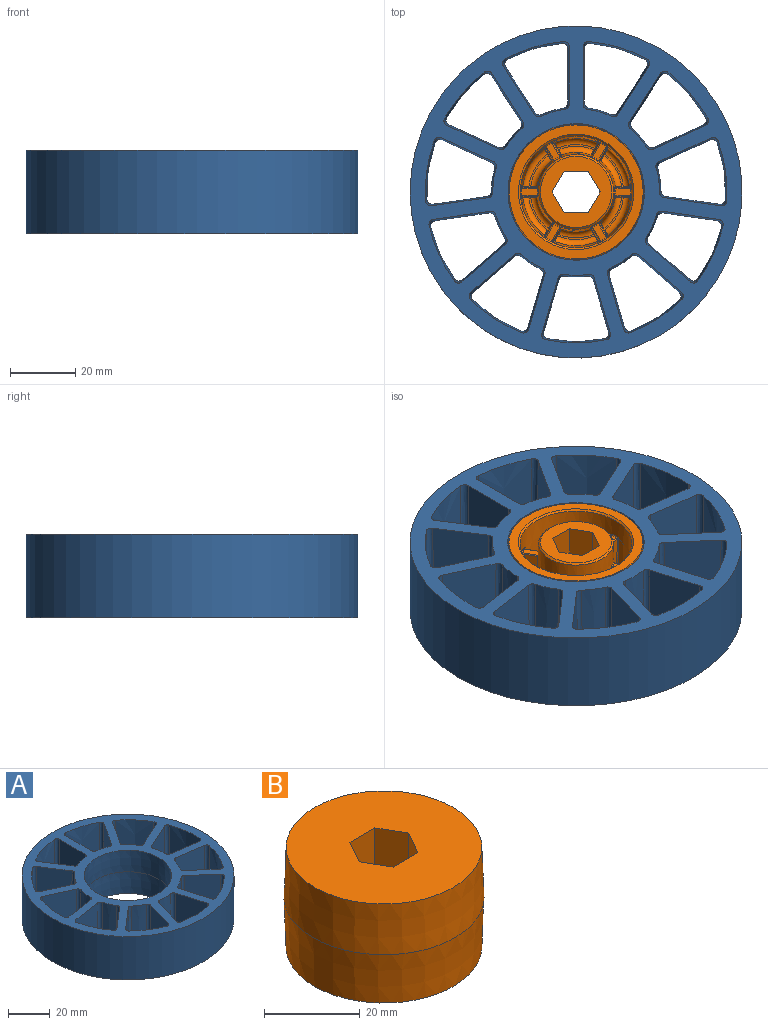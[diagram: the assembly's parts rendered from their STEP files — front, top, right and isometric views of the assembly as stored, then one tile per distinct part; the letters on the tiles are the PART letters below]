
ASSEMBLY  parts=2 mates=1
PART A: 93 faces, bbox 101.7x101.7x25.8 mm
  f0: cylinder r=50.8mm len=101.6mm, axis (0,0,-1), area 8107.3mm2, adj f25,f27
  f1: cone r=20.96mm half-angle=0.3deg, axis (0,0,1), area 1669.7mm2, adj f2,f27
  f2: cone r=20.89mm half-angle=0.3deg, axis (0,0,-1), area 1669.7mm2, adj f1,f25
  f3: cone r=45.72mm half-angle=1deg, axis (0,0,1), area 460.8mm2, adj f25,f27,f58,f59
  f4: cone r=25.97mm half-angle=1deg, axis (0,0,-1), area 186.1mm2, adj f25,f27,f80,f81
  f5: cone r=25.97mm half-angle=1deg, axis (0,0,-1), area 186.2mm2, adj f25,f27,f88,f89
  f6: cone r=45.72mm half-angle=1deg, axis (0,0,1), area 460.8mm2, adj f25,f27,f90,f91
  f7: cone r=45.72mm half-angle=1deg, axis (0,0,1), area 460.8mm2, adj f25,f27,f82,f83
  f8: cone r=25.97mm half-angle=1deg, axis (0,0,-1), area 186.2mm2, adj f25,f27,f76,f77
  f9: cone r=45.72mm half-angle=1deg, axis (0,0,1), area 460.8mm2, adj f25,f27,f78,f79
  f10: cone r=25.97mm half-angle=1deg, axis (0,0,-1), area 186.2mm2, adj f25,f27,f72,f73
  f11: cone r=45.72mm half-angle=1deg, axis (0,0,1), area 460.8mm2, adj f25,f27,f74,f75
  f12: cone r=25.97mm half-angle=1deg, axis (0,0,-1), area 186.2mm2, adj f25,f27,f68,f69
  f13: cone r=45.72mm half-angle=1deg, axis (0,0,1), area 460.8mm2, adj f25,f27,f70,f71
  f14: cone r=25.97mm half-angle=1deg, axis (0,0,-1), area 186.2mm2, adj f25,f27,f64,f65
  f15: cone r=45.72mm half-angle=1deg, axis (0,0,1), area 460.8mm2, adj f25,f27,f66,f67
  f16: cone r=25.97mm half-angle=1deg, axis (0,0,-1), area 186.2mm2, adj f25,f27,f60,f61
  f17: cone r=45.72mm half-angle=1deg, axis (0,0,1), area 460.8mm2, adj f25,f27,f62,f63
  f18: cone r=25.97mm half-angle=1deg, axis (0,0,-1), area 186.2mm2, adj f25,f27,f56,f57
  f19: cone r=25.97mm half-angle=1deg, axis (0,0,-1), area 186.2mm2, adj f25,f27,f52,f53
  f20: cone r=45.72mm half-angle=1deg, axis (0,0,1), area 460.8mm2, adj f25,f27,f54,f55
  f21: cone r=25.97mm half-angle=1deg, axis (0,0,-1), area 186.2mm2, adj f25,f27,f49,f50
  f22: cone r=45.72mm half-angle=1deg, axis (0,0,1), area 460.8mm2, adj f25,f27,f51,f92
  f23: plane 25.4x17.56mm, normal (1,0,0.02), area 435mm2, adj f25,f27,f85,f86
  f24: plane 25.4x17.56mm, normal (-1,0,0.02), area 435mm2, adj f25,f27,f50,f92
  f25: plane 101.66x101.66mm, normal (0,0,1), area 3063.9mm2, adj f0,f2,f3,f4,f5,f6,f7,f8
  f26: cone r=25.97mm half-angle=1deg, axis (0,0,-1), area 186.2mm2, adj f25,f27,f86,f87
  f27: plane 101.66x101.66mm, normal (0,0,-1), area 3415.8mm2, adj f0,f1,f3,f4,f5,f6,f7,f8
  f28: cone r=45.72mm half-angle=1deg, axis (0,0,1), area 460.8mm2, adj f25,f27,f84,f85
  f29: plane 25.4x14.77mm, normal (0.84,0.54,0.02), area 435mm2, adj f25,f27,f49,f51
  f30: plane 25.4x14.77mm, normal (-0.84,-0.54,0.02), area 435mm2, adj f25,f27,f53,f54
  f31: plane 25.4x15.97mm, normal (0.42,0.91,0.02), area 435mm2, adj f25,f27,f52,f55
  f32: plane 25.4x15.97mm, normal (-0.42,-0.91,0.02), area 435mm2, adj f25,f27,f57,f58
  f33: plane 25.4x17.38mm, normal (-0.14,0.99,0.02), area 435mm2, adj f25,f27,f56,f59
  f34: plane 25.4x17.38mm, normal (0.14,-0.99,0.02), area 435mm2, adj f25,f27,f61,f62
  f35: plane 25.4x13.27mm, normal (-0.65,0.76,0.02), area 435mm2, adj f25,f27,f60,f63
  f36: plane 25.4x13.27mm, normal (0.65,-0.76,0.02), area 435mm2, adj f25,f27,f65,f66
  f37: plane 25.4x16.85mm, normal (-0.96,0.28,0.02), area 435mm2, adj f25,f27,f64,f67
  f38: plane 25.4x16.85mm, normal (0.96,-0.28,0.02), area 435mm2, adj f25,f27,f69,f70
  f39: plane 25.4x16.85mm, normal (-0.96,-0.28,0.02), area 435mm2, adj f25,f27,f68,f71
  f40: plane 25.4x16.85mm, normal (0.96,0.28,0.02), area 435mm2, adj f25,f27,f73,f74
  f41: plane 25.4x13.27mm, normal (-0.65,-0.76,0.02), area 435mm2, adj f25,f27,f72,f75
  f42: plane 25.4x13.27mm, normal (0.65,0.76,0.02), area 435mm2, adj f25,f27,f77,f78
  f43: plane 25.4x17.38mm, normal (-0.14,-0.99,0.02), area 435mm2, adj f25,f27,f76,f79
  f44: plane 25.4x17.38mm, normal (0.14,0.99,0.02), area 435mm2, adj f25,f27,f81,f82
  f45: plane 25.4x15.97mm, normal (0.42,-0.91,0.02), area 435mm2, adj f25,f27,f80,f83
  f46: plane 25.4x15.97mm, normal (-0.42,0.91,0.02), area 435mm2, adj f25,f27,f89,f90
  f47: plane 25.4x14.77mm, normal (0.84,-0.54,0.02), area 435mm2, adj f25,f27,f88,f91
  f48: plane 25.4x14.77mm, normal (-0.84,0.54,0.02), area 435mm2, adj f25,f27,f84,f87
  f49: bspline ~25.41x2.15mm, area 57.6mm2, adj f21,f25,f27,f29
  f50: bspline ~25.41x1.96mm, area 57.6mm2, adj f21,f24,f25,f27
  f51: bspline ~25.41x2.43mm, area 66.9mm2, adj f22,f25,f27,f29
  f52: bspline ~25.41x2.17mm, area 57.6mm2, adj f19,f25,f27,f31
  f53: bspline ~25.41x2.15mm, area 57.6mm2, adj f19,f25,f27,f30
  f54: bspline ~25.75x2.43mm, area 66.9mm2, adj f20,f25,f27,f30
  f55: bspline ~25.75x2.44mm, area 66.9mm2, adj f20,f25,f27,f31
  f56: bspline ~25.73x1.95mm, area 57.6mm2, adj f18,f25,f27,f33
  f57: bspline ~25.73x2.13mm, area 57.6mm2, adj f18,f25,f27,f32
  f58: bspline ~25.75x2.41mm, area 66.9mm2, adj f3,f25,f27,f32
  f59: bspline ~25.41x2.23mm, area 66.9mm2, adj f3,f25,f27,f33
  f60: bspline ~25.73x2.13mm, area 57.6mm2, adj f16,f25,f27,f35
  f61: bspline ~25.41x2.07mm, area 57.6mm2, adj f16,f25,f27,f34
  f62: bspline ~25.41x2.31mm, area 66.9mm2, adj f17,f25,f27,f34
  f63: bspline ~25.75x2.4mm, area 66.9mm2, adj f17,f25,f27,f35
  f64: bspline ~25.73x2.14mm, area 57.6mm2, adj f14,f25,f27,f37
  f65: bspline ~25.73x2.09mm, area 57.6mm2, adj f14,f25,f27,f36
  f66: bspline ~25.41x2.36mm, area 66.9mm2, adj f15,f25,f27,f36
  f67: bspline ~25.75x2.4mm, area 66.9mm2, adj f15,f25,f27,f37
  f68: bspline ~25.41x2.05mm, area 57.6mm2, adj f12,f25,f27,f39
  f69: bspline ~25.41x2.05mm, area 57.6mm2, adj f12,f25,f27,f38
  f70: bspline ~25.41x2.34mm, area 66.9mm2, adj f13,f25,f27,f38
  f71: bspline ~25.41x2.34mm, area 66.9mm2, adj f13,f25,f27,f39
  f72: bspline ~25.73x2.09mm, area 57.6mm2, adj f10,f25,f27,f41
  f73: bspline ~25.73x2.14mm, area 57.6mm2, adj f10,f25,f27,f40
  f74: bspline ~25.75x2.4mm, area 66.9mm2, adj f11,f25,f27,f40
  f75: bspline ~25.41x2.36mm, area 66.9mm2, adj f11,f25,f27,f41
  f76: bspline ~25.41x2.07mm, area 57.6mm2, adj f8,f25,f27,f43
  f77: bspline ~25.73x2.13mm, area 57.6mm2, adj f8,f25,f27,f42
  f78: bspline ~25.75x2.4mm, area 66.9mm2, adj f9,f25,f27,f42
  f79: bspline ~25.41x2.31mm, area 66.9mm2, adj f9,f25,f27,f43
  f80: bspline ~25.73x2.13mm, area 57.6mm2, adj f4,f25,f27,f45
  f81: bspline ~25.41x1.94mm, area 57.6mm2, adj f4,f25,f27,f44
  f82: bspline ~25.41x2.23mm, area 66.9mm2, adj f7,f25,f27,f44
  f83: bspline ~25.75x2.41mm, area 66.9mm2, adj f7,f25,f27,f45
  f84: bspline ~25.41x2.43mm, area 66.9mm2, adj f25,f27,f28,f48
  f85: bspline ~25.41x2.18mm, area 66.9mm2, adj f23,f25,f27,f28
  f86: bspline ~25.41x1.96mm, area 57.6mm2, adj f23,f25,f26,f27
  f87: bspline ~25.41x2.15mm, area 57.6mm2, adj f25,f26,f27,f48
  f88: bspline ~25.41x2.15mm, area 57.6mm2, adj f5,f25,f27,f47
  f89: bspline ~25.41x2.17mm, area 57.6mm2, adj f5,f25,f27,f46
  f90: bspline ~25.75x2.44mm, area 66.9mm2, adj f6,f25,f27,f46
  f91: bspline ~25.75x2.43mm, area 66.9mm2, adj f6,f25,f27,f47
  f92: bspline ~25.41x2.18mm, area 66.9mm2, adj f22,f24,f25,f27
PART B: 159 faces, bbox 41.9x41.9x25.4 mm
  f0: torus R=16.68mm, axis (0,0,1), area 0.8mm2, adj f6,f31,f40,f45
  f1: torus R=11.9mm, axis (0,0,1), area 0.8mm2, adj f7,f31,f36,f41
  f2: cone r=20.24mm half-angle=2deg, axis (0,0,-1), area 1655.4mm2, adj f3,f25
  f3: cone r=20.96mm half-angle=2deg, axis (0,0,1), area 1655.4mm2, adj f2,f26
  f4: cone r=10.9mm half-angle=47deg, axis (0,0,1), area 52.3mm2, adj f7,f24
  f5: cone r=17.13mm half-angle=45deg, axis (0,0,-1), area 81.3mm2, adj f6,f26
  f6: cone r=16.46mm half-angle=2deg, axis (0,0,-1), area 1757.7mm2, adj f0,f5,f9,f12,f15,f18,f21,f27
  f7: cone r=11.43mm half-angle=2deg, axis (0,0,1), area 1163.6mm2, adj f1,f4,f8,f11,f14,f17,f20,f23
  f8: torus R=14.02mm, axis (0,0,-1), area 29mm2, adj f7,f10,f32,f146
  f9: torus R=14.55mm, axis (0,0,-1), area 37.6mm2, adj f6,f10,f35,f151
  f10: plane 9.83x5.94mm, normal (0,0,-1), area 6mm2, adj f8,f9,f33,f149
  f11: torus R=14.02mm, axis (0,0,-1), area 29mm2, adj f7,f13,f128,f135
  f12: torus R=14.55mm, axis (0,0,-1), area 37.6mm2, adj f6,f13,f133,f138
  f13: plane 11.35x1.61mm, normal (0,0,-1), area 6mm2, adj f11,f12,f131,f136
  f14: torus R=14.02mm, axis (0,0,-1), area 29mm2, adj f7,f16,f110,f117
  f15: torus R=14.55mm, axis (0,0,-1), area 37.6mm2, adj f6,f16,f115,f120
  f16: plane 9.83x5.94mm, normal (0,0,-1), area 6mm2, adj f14,f15,f113,f118
  f17: torus R=14.02mm, axis (0,0,-1), area 29mm2, adj f7,f19,f92,f99
  f18: torus R=14.55mm, axis (0,0,-1), area 37.6mm2, adj f6,f19,f97,f102
  f19: plane 9.83x5.94mm, normal (0,0,-1), area 6mm2, adj f17,f18,f95,f100
  f20: torus R=14.02mm, axis (0,0,-1), area 29mm2, adj f7,f22,f74,f81
  f21: torus R=14.55mm, axis (0,0,-1), area 37.6mm2, adj f6,f22,f79,f84
  f22: plane 11.35x1.61mm, normal (0,0,-1), area 6mm2, adj f20,f21,f77,f82
  f23: torus R=14.02mm, axis (0,0,-1), area 29mm2, adj f7,f28,f42,f63
  f24: plane 21.81x21.81mm, normal (0,0,-1), area 232.7mm2, adj f4,f153,f154,f155,f156,f157,f158
  f25: plane 41.02x41.02mm, normal (0,0,1), area 1180.9mm2, adj f2,f153,f154,f155,f156,f157,f158
  f26: plane 41.02x41.02mm, normal (0,0,-1), area 342.7mm2, adj f3,f5
  f27: torus R=14.55mm, axis (0,0,-1), area 37.6mm2, adj f6,f28,f46,f66
  f28: plane 9.83x5.94mm, normal (0,0,-1), area 6mm2, adj f23,f27,f44,f64
  f29: plane 14.75x4.78mm, normal (0,-1,-0.02), area 61.7mm2, adj f39,f42,f43,f44,f46,f47
  f30: plane 14.74x4.78mm, normal (0,1,-0.02), area 61.7mm2, adj f32,f33,f34,f35,f37,f38
  f31: plane 4.82x2.04mm, normal (0,0,-1), area 9.8mm2, adj f0,f1,f38,f43
  f32: bspline ~1.91x1.84mm, area 1mm2, adj f8,f30,f33,f34
  f33: cylinder r=0.25mm len=0.53mm, axis (-1,0,0), area 0.2mm2, adj f10,f30,f32,f35
  f34: bspline ~13.15x0.68mm, area 4.8mm2, adj f7,f30,f32,f36
  f35: bspline ~1.95x1.85mm, area 1.2mm2, adj f9,f30,f33,f37
  f36: bspline ~0.5x0.5mm, area 0.2mm2, adj f1,f7,f34,f38
  f37: bspline ~13.15x0.74mm, area 5.6mm2, adj f6,f30,f35,f40
  f38: cylinder r=0.25mm len=4.83mm, axis (-1,0,0), area 1.9mm2, adj f30,f31,f36,f40
  f39: cylinder r=0.25mm len=13.15mm, axis (0.03,-0.02,1), area 4.8mm2, adj f7,f29,f41,f42
  f40: bspline ~0.53x0.51mm, area 0.2mm2, adj f0,f6,f37,f38
  f41: bspline ~0.5x0.5mm, area 0.2mm2, adj f1,f7,f39,f43
  f42: bspline ~1.91x1.84mm, area 1mm2, adj f23,f29,f39,f44
  f43: cylinder r=0.25mm len=4.83mm, axis (1,0,0), area 1.9mm2, adj f29,f31,f41,f45
  f44: cylinder r=0.25mm len=0.53mm, axis (1,0,0), area 0.2mm2, adj f28,f29,f42,f46
  f45: bspline ~0.53x0.51mm, area 0.2mm2, adj f0,f6,f43,f47
  f46: bspline ~1.95x1.85mm, area 1.2mm2, adj f27,f29,f44,f47
  f47: bspline ~13.15x0.74mm, area 5.6mm2, adj f6,f29,f45,f46
  f48: plane 14.75x4.14mm, normal (-0.87,-0.5,-0.02), area 61.7mm2, adj f71,f74,f76,f77,f79,f80
  f49: plane 14.74x4.14mm, normal (0.87,0.5,-0.02), area 61.7mm2, adj f63,f64,f65,f66,f68,f69
  f50: plane 5.17x4.16mm, normal (0,0,-1), area 9.8mm2, adj f69,f70,f75,f76
  f51: plane 14.75x4.14mm, normal (-0.87,0.5,-0.02), area 61.7mm2, adj f89,f92,f94,f95,f97,f98
  f52: plane 14.74x4.14mm, normal (0.87,-0.5,-0.02), area 61.7mm2, adj f81,f82,f83,f84,f86,f87
  f53: plane 5.17x4.16mm, normal (0,0,-1), area 9.8mm2, adj f87,f88,f93,f94
  f54: plane 14.75x4.78mm, normal (0,1,-0.02), area 61.7mm2, adj f107,f110,f112,f113,f115,f116
  f55: plane 14.74x4.78mm, normal (0,-1,-0.02), area 61.7mm2, adj f99,f100,f101,f102,f104,f105
  f56: plane 4.82x2.04mm, normal (0,0,-1), area 9.8mm2, adj f105,f106,f111,f112
  f57: plane 14.75x4.14mm, normal (0.87,0.5,-0.02), area 61.7mm2, adj f125,f128,f130,f131,f133,f134
  f58: plane 14.74x4.14mm, normal (-0.87,-0.5,-0.02), area 61.7mm2, adj f117,f118,f119,f120,f122,f123
  f59: plane 5.17x4.16mm, normal (0,0,-1), area 9.8mm2, adj f123,f124,f129,f130
  f60: plane 14.75x4.14mm, normal (0.87,-0.5,-0.02), area 61.7mm2, adj f143,f146,f148,f149,f151,f152
  f61: plane 14.74x4.14mm, normal (-0.87,0.5,-0.02), area 61.7mm2, adj f135,f136,f137,f138,f140,f141
  f62: plane 5.17x4.16mm, normal (0,0,-1), area 9.8mm2, adj f141,f142,f147,f148
  f63: bspline ~1.84x1.75mm, area 1mm2, adj f23,f49,f64,f65
  f64: cylinder r=0.25mm len=0.59mm, axis (-0.5,0.87,0), area 0.2mm2, adj f28,f49,f63,f66
  f65: bspline ~13.15x0.59mm, area 4.8mm2, adj f7,f49,f63,f67
  f66: bspline ~1.85x1.83mm, area 1.2mm2, adj f27,f49,f64,f68
  f67: bspline ~0.5x0.49mm, area 0.2mm2, adj f7,f65,f69,f70
  f68: bspline ~13.15x0.66mm, area 5.6mm2, adj f6,f49,f66,f72
  f69: cylinder r=0.25mm len=4.31mm, axis (-0.5,0.87,0), area 1.9mm2, adj f49,f50,f67,f72
  f70: torus R=11.9mm, axis (0,0,1), area 0.8mm2, adj f7,f50,f67,f73
  f71: cylinder r=0.25mm len=13.15mm, axis (0,-0.04,1), area 4.8mm2, adj f7,f48,f73,f74
  f72: bspline ~0.56x0.51mm, area 0.2mm2, adj f6,f68,f69,f75
  f73: bspline ~0.56x0.5mm, area 0.2mm2, adj f7,f70,f71,f76
  f74: bspline ~1.84x1.77mm, area 1mm2, adj f20,f48,f71,f77
  f75: torus R=16.68mm, axis (0,0,1), area 0.8mm2, adj f6,f50,f72,f78
  f76: cylinder r=0.25mm len=4.31mm, axis (0.5,-0.87,0), area 1.9mm2, adj f48,f50,f73,f78
  f77: cylinder r=0.25mm len=0.59mm, axis (0.5,-0.87,0), area 0.2mm2, adj f22,f48,f74,f79
  f78: bspline ~0.51x0.48mm, area 0.2mm2, adj f6,f75,f76,f80
  f79: bspline ~1.85x1.79mm, area 1.2mm2, adj f21,f48,f77,f80
  f80: bspline ~13.16x0.7mm, area 5.6mm2, adj f6,f48,f78,f79
  f81: bspline ~1.84x1.77mm, area 1mm2, adj f20,f52,f82,f83
  f82: cylinder r=0.25mm len=0.59mm, axis (-0.5,-0.87,0), area 0.2mm2, adj f22,f52,f81,f84
  f83: bspline ~13.15x0.61mm, area 4.8mm2, adj f7,f52,f81,f85
  f84: bspline ~1.85x1.79mm, area 1.2mm2, adj f21,f52,f82,f86
  f85: bspline ~0.56x0.5mm, area 0.2mm2, adj f7,f83,f87,f88
  f86: bspline ~13.15x0.66mm, area 5.6mm2, adj f6,f52,f84,f90
  f87: cylinder r=0.25mm len=4.31mm, axis (0.5,0.87,0), area 1.9mm2, adj f52,f53,f85,f90
  f88: torus R=11.9mm, axis (0,0,1), area 0.8mm2, adj f7,f53,f85,f91
  f89: cylinder r=0.25mm len=13.15mm, axis (-0.03,-0.02,1), area 4.8mm2, adj f7,f51,f91,f92
  f90: bspline ~0.51x0.48mm, area 0.2mm2, adj f6,f86,f87,f93
  f91: bspline ~0.5x0.49mm, area 0.2mm2, adj f7,f88,f89,f94
  f92: bspline ~1.84x1.75mm, area 1mm2, adj f17,f51,f89,f95
  f93: torus R=16.68mm, axis (0,0,1), area 0.8mm2, adj f6,f53,f90,f96
  f94: cylinder r=0.25mm len=4.31mm, axis (-0.5,-0.87,0), area 1.9mm2, adj f51,f53,f91,f96
  f95: cylinder r=0.25mm len=0.59mm, axis (0.5,0.87,0), area 0.2mm2, adj f19,f51,f92,f97
  f96: bspline ~0.56x0.51mm, area 0.2mm2, adj f6,f93,f94,f98
  f97: bspline ~1.85x1.83mm, area 1.2mm2, adj f18,f51,f95,f98
  f98: bspline ~13.15x0.66mm, area 5.6mm2, adj f6,f51,f96,f97
  f99: bspline ~1.91x1.84mm, area 1mm2, adj f17,f55,f100,f101
  f100: cylinder r=0.25mm len=0.53mm, axis (-1,0,0), area 0.2mm2, adj f19,f55,f99,f102
  f101: bspline ~13.15x0.68mm, area 4.8mm2, adj f7,f55,f99,f103
  f102: bspline ~1.95x1.85mm, area 1.2mm2, adj f18,f55,f100,f104
  f103: bspline ~0.5x0.5mm, area 0.2mm2, adj f7,f101,f105,f106
  f104: bspline ~13.15x0.74mm, area 5.6mm2, adj f6,f55,f102,f108
  f105: cylinder r=0.25mm len=4.83mm, axis (1,0,0), area 1.9mm2, adj f55,f56,f103,f108
  f106: torus R=11.9mm, axis (0,0,1), area 0.8mm2, adj f7,f56,f103,f109
  f107: cylinder r=0.25mm len=13.15mm, axis (-0.03,0.02,1), area 4.8mm2, adj f7,f54,f109,f110
  f108: bspline ~0.53x0.51mm, area 0.2mm2, adj f6,f104,f105,f111
  f109: bspline ~0.5x0.5mm, area 0.2mm2, adj f7,f106,f107,f112
  f110: bspline ~1.91x1.84mm, area 1mm2, adj f14,f54,f107,f113
  f111: torus R=16.68mm, axis (0,0,1), area 0.8mm2, adj f6,f56,f108,f114
  f112: cylinder r=0.25mm len=4.83mm, axis (-1,0,0), area 1.9mm2, adj f54,f56,f109,f114
  f113: cylinder r=0.25mm len=0.53mm, axis (1,0,0), area 0.2mm2, adj f16,f54,f110,f115
  f114: bspline ~0.53x0.51mm, area 0.2mm2, adj f6,f111,f112,f116
  f115: bspline ~1.95x1.85mm, area 1.2mm2, adj f15,f54,f113,f116
  f116: bspline ~13.15x0.74mm, area 5.6mm2, adj f6,f54,f114,f115
  f117: bspline ~1.84x1.75mm, area 1mm2, adj f14,f58,f118,f119
  f118: cylinder r=0.25mm len=0.59mm, axis (-0.5,0.87,0), area 0.2mm2, adj f16,f58,f117,f120
  f119: bspline ~13.15x0.59mm, area 4.8mm2, adj f7,f58,f117,f121
  f120: bspline ~1.85x1.83mm, area 1.2mm2, adj f15,f58,f118,f122
  f121: bspline ~0.5x0.49mm, area 0.2mm2, adj f7,f119,f123,f124
  f122: bspline ~13.15x0.66mm, area 5.6mm2, adj f6,f58,f120,f126
  f123: cylinder r=0.25mm len=4.31mm, axis (0.5,-0.87,0), area 1.9mm2, adj f58,f59,f121,f126
  f124: torus R=11.9mm, axis (0,0,1), area 0.8mm2, adj f7,f59,f121,f127
  f125: cylinder r=0.25mm len=13.15mm, axis (0,0.04,1), area 4.8mm2, adj f7,f57,f127,f128
  f126: bspline ~0.56x0.51mm, area 0.2mm2, adj f6,f122,f123,f129
  f127: bspline ~0.56x0.5mm, area 0.2mm2, adj f7,f124,f125,f130
  f128: bspline ~1.84x1.77mm, area 1mm2, adj f11,f57,f125,f131
  f129: torus R=16.68mm, axis (0,0,1), area 0.8mm2, adj f6,f59,f126,f132
  f130: cylinder r=0.25mm len=4.31mm, axis (-0.5,0.87,0), area 1.9mm2, adj f57,f59,f127,f132
  f131: cylinder r=0.25mm len=0.59mm, axis (0.5,-0.87,0), area 0.2mm2, adj f13,f57,f128,f133
  f132: bspline ~0.51x0.48mm, area 0.2mm2, adj f6,f129,f130,f134
  f133: bspline ~1.85x1.79mm, area 1.2mm2, adj f12,f57,f131,f134
  f134: bspline ~13.16x0.7mm, area 5.6mm2, adj f6,f57,f132,f133
  f135: bspline ~1.84x1.77mm, area 1mm2, adj f11,f61,f136,f137
  f136: cylinder r=0.25mm len=0.59mm, axis (0.5,0.87,0), area 0.2mm2, adj f13,f61,f135,f138
  f137: bspline ~13.15x0.68mm, area 4.8mm2, adj f7,f61,f135,f139
  f138: bspline ~1.85x1.79mm, area 1.2mm2, adj f12,f61,f136,f140
  f139: bspline ~0.56x0.5mm, area 0.2mm2, adj f7,f137,f141,f142
  f140: bspline ~13.15x0.66mm, area 5.6mm2, adj f6,f61,f138,f144
  f141: cylinder r=0.25mm len=4.31mm, axis (-0.5,-0.87,0), area 1.9mm2, adj f61,f62,f139,f144
  f142: torus R=11.9mm, axis (0,0,1), area 0.8mm2, adj f7,f62,f139,f145
  f143: cylinder r=0.25mm len=13.15mm, axis (0.03,0.02,1), area 4.8mm2, adj f7,f60,f145,f146
  f144: bspline ~0.51x0.48mm, area 0.2mm2, adj f6,f140,f141,f147
  f145: bspline ~0.5x0.49mm, area 0.2mm2, adj f7,f142,f143,f148
  f146: bspline ~1.84x1.75mm, area 1mm2, adj f8,f60,f143,f149
  f147: torus R=16.68mm, axis (0,0,1), area 0.8mm2, adj f6,f62,f144,f150
  f148: cylinder r=0.25mm len=4.31mm, axis (0.5,0.87,0), area 1.9mm2, adj f60,f62,f145,f150
  f149: cylinder r=0.25mm len=0.59mm, axis (-0.5,-0.87,0), area 0.2mm2, adj f10,f60,f146,f151
  f150: bspline ~0.56x0.51mm, area 0.2mm2, adj f6,f147,f148,f152
  f151: bspline ~1.85x1.83mm, area 1.2mm2, adj f9,f60,f149,f152
  f152: bspline ~13.15x0.66mm, area 5.6mm2, adj f6,f60,f150,f151
  f153: plane 25.4x6.38mm, normal (0.87,0.5,0), area 187mm2, adj f24,f25,f154,f158
  f154: plane 25.4x7.36mm, normal (0,1,0), area 187mm2, adj f24,f25,f153,f155
  f155: plane 25.4x6.38mm, normal (-0.87,0.5,0), area 187mm2, adj f24,f25,f154,f156
  f156: plane 25.4x6.38mm, normal (-0.87,-0.5,0), area 187mm2, adj f24,f25,f155,f157
  f157: plane 25.4x7.36mm, normal (0,-1,0), area 187mm2, adj f24,f25,f156,f158
  f158: plane 25.4x6.38mm, normal (0.87,-0.5,0), area 187mm2, adj f24,f25,f153,f157
PLACE A t=(1.42,1.11,20.38)mm
PLACE B rot(axis=(0,1,0),180deg) t=(1.42,1.11,7.68)mm
MATE fastened B.f5 <-> A.f0  axis (0,0,-1) through (1.42,1.11,-5.02)mm
